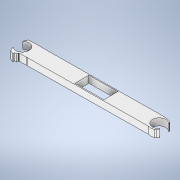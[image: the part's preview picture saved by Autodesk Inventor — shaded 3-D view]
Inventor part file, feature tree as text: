
AUTODESK INVENTOR PART (.ipt)
format: ipt  version: 2022 (Build 260153000, 153)  size: 333,824 bytes
history: native  units: mm
features: extrude x1, sketch x1
ambient origin geometry x8: Origin, YZ Plane, XZ Plane, XY Plane, X Axis, Y Axis, Z Axis, Center Point
bodies: Body1 (feature_tree)
feature tree (2):
  extrude  "Extrusion6"  Depth=20.0mm
  sketch  "Sketch1"  dims[d31=34.456mm d50=368.759386mm d57=16.0mm d69=8.0mm d70=23.0mm d71=8.0mm d73=16.0mm d80=19.0mm d81=16.0mm d82=1.0mm d83=1.0mm d84=1.0mm d85=1.0mm d86=1.0mm d87=0.8mm d88=1.0mm d90=19.0mm d94=5.0mm d95=5.0mm d105=5.0mm d106=5.0mm d108=2.0mm d109=19.0mm d114=5.0mm d115=5.0mm d116=24.0mm d117=2.5mm d118=2.5mm d123=2.5mm d124=2.5mm d125=10.0mm d126=24.0mm d127=24.0mm d128=27.0mm d135=0.5mm d136=45.0deg d139=7.0mm d165=45.0deg d169=27.0mm d175=90.0deg d181=45.0deg d185=7.0mm d186=45.0deg d190=7.0mm d191=45.0deg d197=90.0deg d203=90.0deg d206=7.0mm d209=40.0mm d210=10.0mm d211=0.0mm d212=41.0mm d213=20.0mm d214=23.0mm]
